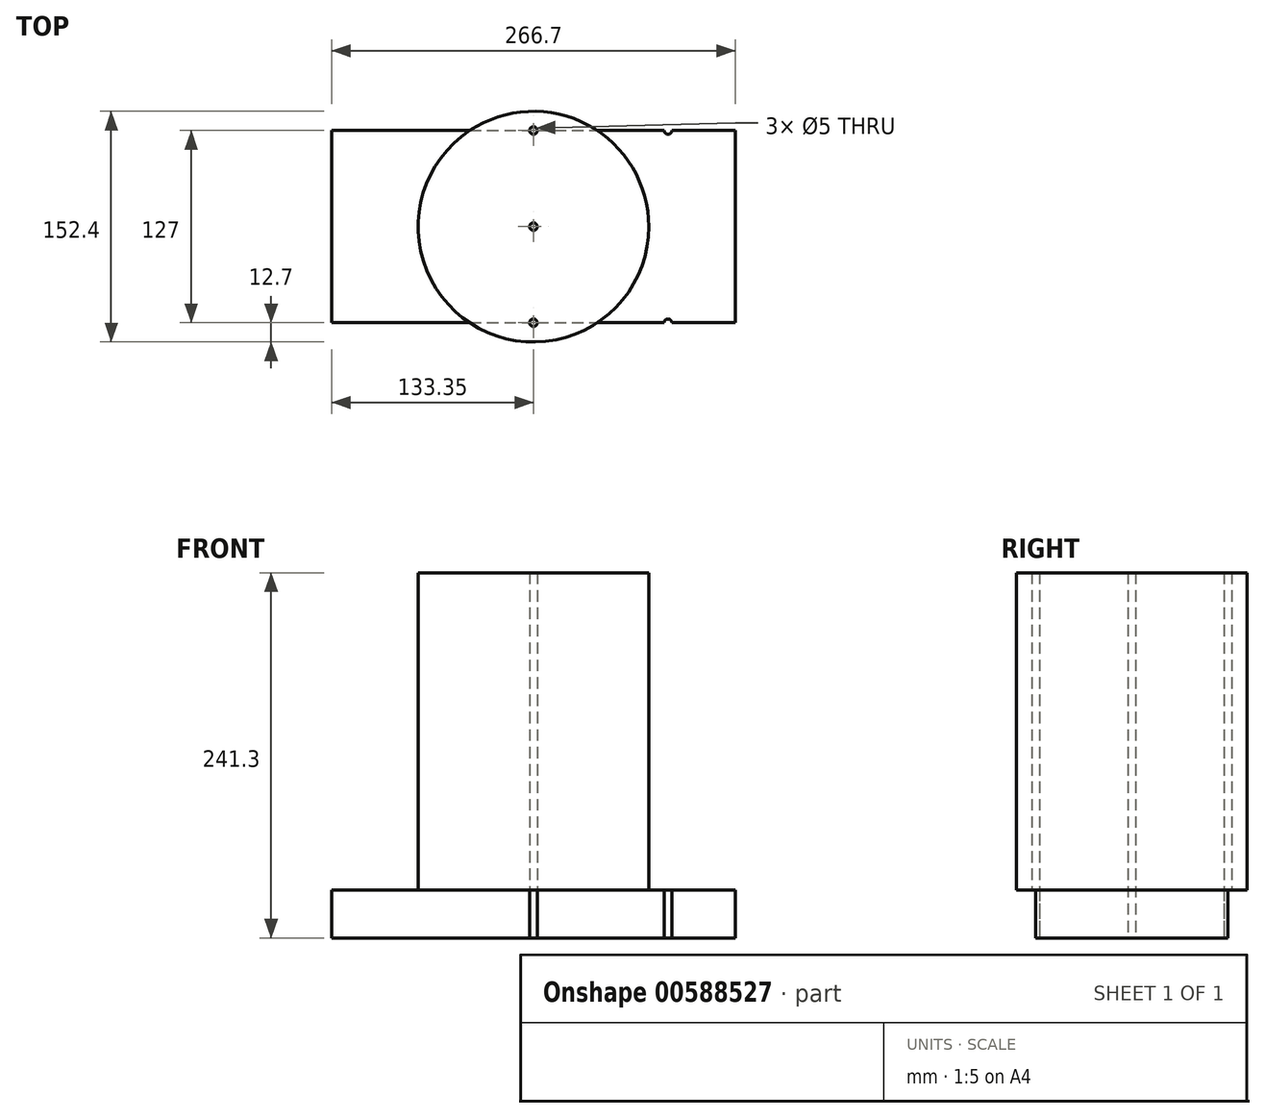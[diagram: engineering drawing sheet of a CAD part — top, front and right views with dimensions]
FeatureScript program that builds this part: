
annotation { "Feature Type Name" : "Feature", "Feature Type Description" : "" }
export const myFeature = defineFeature(function(context is Context, id is Id, definition is map)
    precondition{}
    {
        {
            var Q0;
            Q0=qCreatedBy(makeId("Top.planeOp"),FACE);
            var sketch = newSketch(context, id + "F0", { "sketchPlane" : qUnion([Q0])});
            skLineSegment(sketch, "E0.bottom", {"start": v(-133.35, 63.5) * mm, "end": v(133.35, 63.5) * mm});
            skLineSegment(sketch, "E0.top", {"start": v(-133.35, -63.5) * mm, "end": v(133.35, -63.5) * mm});
            skLineSegment(sketch, "E0.left", {"start": v(-133.35, 63.5) * mm, "end": v(-133.35, -63.5) * mm});
            skLineSegment(sketch, "E0.right", {"start": v(133.35, 63.5) * mm, "end": v(133.35, -63.5) * mm});
            skPoint(sketch, "E0.middle", {"position": v(0, 0) * mm});
            skPoint(sketch, "E1", {"position": v(88.9, 63.5) * mm});
            skPoint(sketch, "E2", {"position": v(88.9, -63.5) * mm});
            skPoint(sketch, "E3", {"position": v(0, 63.5) * mm});
            skPoint(sketch, "E4", {"position": v(0, -63.5) * mm});
            skSolve(sketch);
        }
        {
            var Q0;
            Q0 = qSketchRegion(id + "F0", true);
            extrude(context, id + "F1", {"entities" : qUnion([Q0]), "depth" : 31.75 * mm, "offsetDistance" : 25.4 * mm});
        }
        {
            var Q0;
            Q0=makeQuery(id+"F1.opExtrude","CAP_FACE",FACE,{"disambiguationData":[OSD([sQuery(id+"F0.wireOp",EDGE,"E0.bottom"),sQuery(id+"F0.wireOp",EDGE,"E0.top"),sQuery(id+"F0.wireOp",EDGE,"E0.left"),sQuery(id+"F0.wireOp",EDGE,"E0.right")])],"isStart":false});
            var sketch = newSketch(context, id + "F2", { "sketchPlane" : qUnion([Q0])});
            skCircle(sketch, "E5", {"center": v(0, 0) * mm, "radius": 76.2 * mm});
            skSolve(sketch);
        }
        {
            var Q0;
            {var subQ0=sQuery(id+"F2.wireOp",EDGE,"E5");var subQ1=makeQuery(id+"F1.opExtrude","CAP_EDGE",EDGE,{"disambiguationData":[OSD([sQuery(id+"F0.wireOp",EDGE,"E0.bottom")])],"isStart":false});var subQ2=makeQuery(id+"F2.imprint","INTERSECT",VERTEX,{"disambiguationData":[OD(0.0)],"derivedFrom":[subQ1,subQ0]});Q0=makeQuery(id+"F2.imprint","IMPRINT",FACE,{"disambiguationData":[TD([[makeQuery(id+"F2.imprint","IMPRINT",EDGE,{"disambiguationData":[TD([[subQ2,1.0]])],"derivedFrom":subQ0}),1.0]])]});}
            var Q1;
            {var subQ0=sQuery(id+"F2.wireOp",EDGE,"E5");var subQ1=makeQuery(id+"F1.opExtrude","CAP_EDGE",EDGE,{"disambiguationData":[OSD([sQuery(id+"F0.wireOp",EDGE,"E0.bottom")])],"isStart":false});var subQ2=makeQuery(id+"F2.imprint","INTERSECT",VERTEX,{"disambiguationData":[OD(0.0)],"derivedFrom":[subQ1,subQ0]});Q1=makeQuery(id+"F2.imprint","IMPRINT",FACE,{"disambiguationData":[TD([[makeQuery(id+"F2.imprint","IMPRINT",EDGE,{"disambiguationData":[TD([[subQ2,-1.0]])],"derivedFrom":subQ0}),1.0]])]});}
            var Q2;
            {var subQ0=sQuery(id+"F2.wireOp",EDGE,"E5");var subQ1=makeQuery(id+"F1.opExtrude","CAP_EDGE",EDGE,{"disambiguationData":[OSD([sQuery(id+"F0.wireOp",EDGE,"E0.top")])],"isStart":false});var subQ2=makeQuery(id+"F2.imprint","INTERSECT",VERTEX,{"disambiguationData":[OD(0.0)],"derivedFrom":[subQ1,subQ0]});Q2=makeQuery(id+"F2.imprint","IMPRINT",FACE,{"disambiguationData":[TD([[makeQuery(id+"F2.imprint","IMPRINT",EDGE,{"disambiguationData":[TD([[subQ2,-1.0]])],"derivedFrom":subQ0}),1.0]])]});}
            extrude(context, id + "F3", {"entities" : qUnion([Q0, Q1, Q2]), "operationType" : NewBodyOperationType.ADD, "depth" : 209.55 * mm, "offsetDistance" : 25.4 * mm});
        }
        {
            var Q0;
            Q0=sQuery(id+"F0.wireOp",VERTEX,"E1");
            var Q1;
            Q1=sQuery(id+"F0.wireOp",VERTEX,"E2");
            var Q2;
            Q2=sQuery(id+"F0.wireOp",VERTEX,"E4");
            var Q3;
            Q3=sQuery(id+"F0.wireOp",VERTEX,"E3");
            var Q4;
            Q4=sQuery(id+"F0.wireOp",VERTEX,"E0.middle");
            var Q5;
            Q5=makeQuery(id+"F1.opExtrude","SWEPT_BODY",BODY,{"disambiguationData":[OSD([sQuery(id+"F0.wireOp",EDGE,"E0.bottom"),sQuery(id+"F0.wireOp",EDGE,"E0.top"),sQuery(id+"F0.wireOp",EDGE,"E0.left"),sQuery(id+"F0.wireOp",EDGE,"E0.right")])]});
            hole(context, id + "F4", {"style" : HoleStyle.SIMPLE, "endStyle" : HoleEndStyle.THROUGH, "oppositeDirection" : true, "holeDiameter" : 5 * mm, "majorDiameter" : 6.35 * mm, "isTappedThrough" : true, "tappedDepth" : 12.7 * mm, "tapClearance" : 3, "locations" : qUnion([Q0, Q1, Q2, Q3, Q4]), "scope" : qUnion([Q5])});
        }
    });
